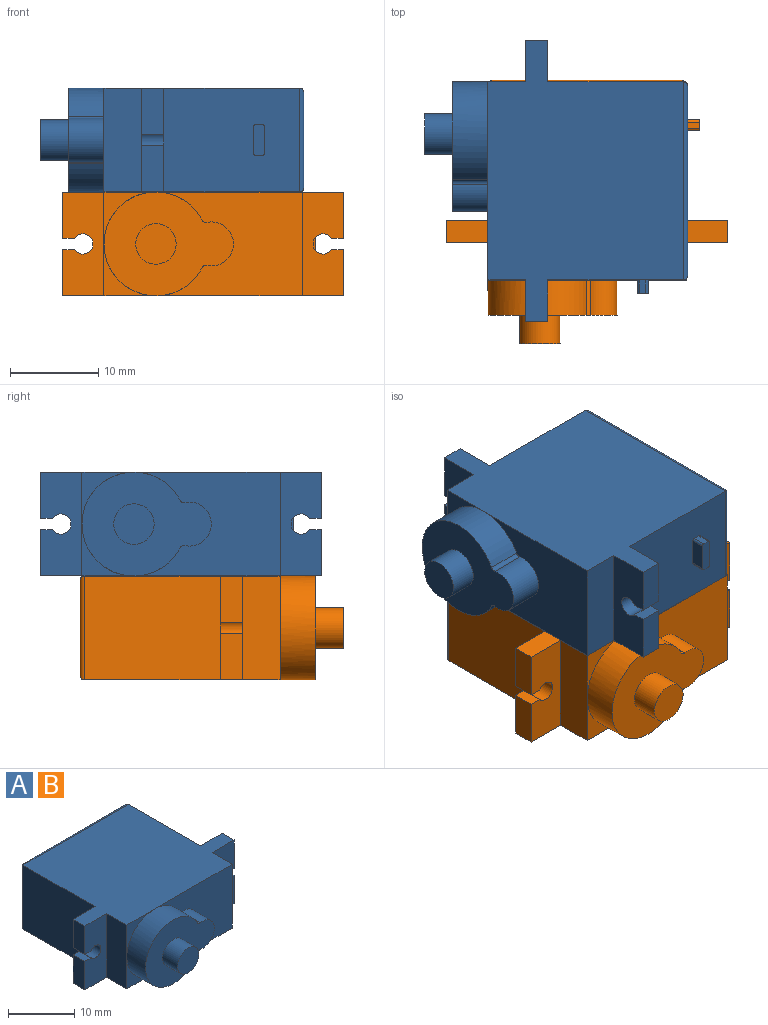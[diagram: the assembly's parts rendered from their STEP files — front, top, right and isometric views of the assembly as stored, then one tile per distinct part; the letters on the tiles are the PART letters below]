
ASSEMBLY  parts=2 mates=1
PART A: 44 faces, bbox 31.9x29.9x11.8 mm
  f0: cylinder r=0.5mm len=22.5mm, axis (-1,0,0), area 17.4mm2, adj f1,f2,f5,f6
  f1: cylinder r=0.5mm len=11.8mm, axis (0,0,-1), area 9mm2, adj f0,f3,f4,f6
  f2: cylinder r=0.5mm len=11.8mm, axis (0,0,-1), area 9mm2, adj f0,f3,f6,f37
  f3: cylinder r=0.5mm len=22.5mm, axis (1,0,0), area 17.4mm2, adj f1,f2,f6,f43
  f4: plane 15.4x11.8mm, normal (-1,0,0), area 181.7mm2, adj f1,f5,f22,f43
  f5: plane 31.9x22.2mm, normal (0,0,-1), area 523mm2, adj f0,f4,f22,f24,f26,f34,f36,f37
  f6: plane 21.5x10.8mm, normal (0,1,0), area 232.2mm2, adj f0,f1,f2,f3
  f7: cylinder r=0.25mm len=1.5mm, axis (-1,0,0), area 0.6mm2, adj f8,f9,f15,f37
  f8: plane 1.5x0.7mm, normal (0,0,1), area 1mm2, adj f7,f9,f10,f37
  f9: plane 3.6x1.2mm, normal (1,0,0), area 4.3mm2, adj f7,f8,f10,f11,f12,f13,f14,f15
  f10: cylinder r=0.25mm len=1.5mm, axis (-1,0,0), area 0.6mm2, adj f8,f9,f11,f37
  f11: plane 3.1x1.5mm, normal (0,1,0), area 4.7mm2, adj f9,f10,f12,f37
  f12: cylinder r=0.25mm len=1.5mm, axis (-1,0,0), area 0.6mm2, adj f9,f11,f13,f37
  f13: plane 1.5x0.7mm, normal (0,0,-1), area 1mm2, adj f9,f12,f14,f37
  f14: cylinder r=0.25mm len=1.5mm, axis (-1,0,0), area 0.6mm2, adj f9,f13,f15,f37
  f15: plane 3.1x1.5mm, normal (0,-1,0), area 4.7mm2, adj f7,f9,f14,f37
  f16: cylinder r=1.15mm len=2.5mm, axis (0,1,0), area 14.6mm2, adj f17,f18,f22,f41
  f17: plane 2.5x1.35mm, normal (0,0,-1), area 3.4mm2, adj f16,f22,f23,f41
  f18: plane 2.5x1.35mm, normal (0,0,1), area 3.4mm2, adj f16,f22,f41,f42
  f19: plane 2.5x1.35mm, normal (0,0,-1), area 3.4mm2, adj f20,f25,f26,f38
  f20: cylinder r=1.15mm len=2.5mm, axis (0,1,0), area 14.6mm2, adj f19,f21,f26,f38
  f21: plane 2.5x1.35mm, normal (0,0,1), area 3.4mm2, adj f20,f24,f26,f38
  f22: plane 11.8x4.7mm, normal (0,1,0), area 49.7mm2, adj f4,f5,f16,f17,f18,f23,f42,f43
  f23: plane 5.25x2.5mm, normal (-1,0,0), area 13.1mm2, adj f17,f22,f41,f43
  f24: plane 5.25x2.5mm, normal (1,0,0), area 13.1mm2, adj f5,f21,f26,f38
  f25: plane 5.25x2.5mm, normal (1,0,0), area 13.1mm2, adj f19,f26,f38,f43
  f26: plane 11.8x4.7mm, normal (0,1,0), area 49.7mm2, adj f5,f19,f20,f21,f24,f25,f37,f43
  f27: cylinder r=2.3mm len=4.6mm, axis (0,1,0), area 46.2mm2, adj f28,f33
  f28: plane 4.6x4.6mm, normal (0,-1,0), area 16.6mm2, adj f27
  f29: cylinder r=0.5mm len=4mm, axis (0,-1,0), area 2.6mm2, adj f30,f32,f33,f36
  f30: cylinder r=5.9mm len=11.8mm, axis (0,1,0), area 125.8mm2, adj f29,f31,f33,f34,f35,f36
  f31: cylinder r=0.5mm len=4mm, axis (0,-1,0), area 2.6mm2, adj f30,f32,f33,f36
  f32: cylinder r=2.5mm len=5mm, axis (0,1,0), area 35.5mm2, adj f29,f31,f33,f36
  f33: plane 14.7x11.8mm, normal (0,-1,0), area 105.4mm2, adj f27,f29,f30,f31,f32
  f34: plane 5.9x5.9mm, normal (0,-1,0), area 7.5mm2, adj f5,f30,f40
  f35: plane 5.9x5.9mm, normal (0,-1,0), area 7.5mm2, adj f30,f40,f43
  f36: plane 16.6x11.8mm, normal (0,-1,0), area 128.5mm2, adj f5,f29,f30,f31,f32,f39,f43
  f37: plane 15.4x11.8mm, normal (1,0,0), area 177.5mm2, adj f2,f5,f7,f8,f10,f11,f12,f13
  f38: plane 11.8x4.7mm, normal (0,-1,0), area 49.7mm2, adj f5,f19,f20,f21,f24,f25,f39,f43
  f39: plane 11.8x4.3mm, normal (1,0,0), area 50.7mm2, adj f5,f36,f38,f43
  f40: plane 11.8x4.3mm, normal (-1,0,0), area 50.7mm2, adj f5,f34,f35,f41,f43
  f41: plane 11.8x4.7mm, normal (0,-1,0), area 49.7mm2, adj f5,f16,f17,f18,f23,f40,f42,f43
  f42: plane 5.25x2.5mm, normal (-1,0,0), area 13.1mm2, adj f5,f18,f22,f41
  f43: plane 31.9x22.2mm, normal (0,0,1), area 523mm2, adj f3,f4,f22,f23,f25,f26,f35,f36
PART B: same geometry as A
PLACE A rot(axis=(0,0,-1),90deg) t=(24.59,15.61,12.07)mm
PLACE B t=(-25.98,12.68,0.27)mm
MATE fastened A.f5 <-> B.f43  axis (0,0,-1) through (-10.48,-22.39,-8.52)mm
